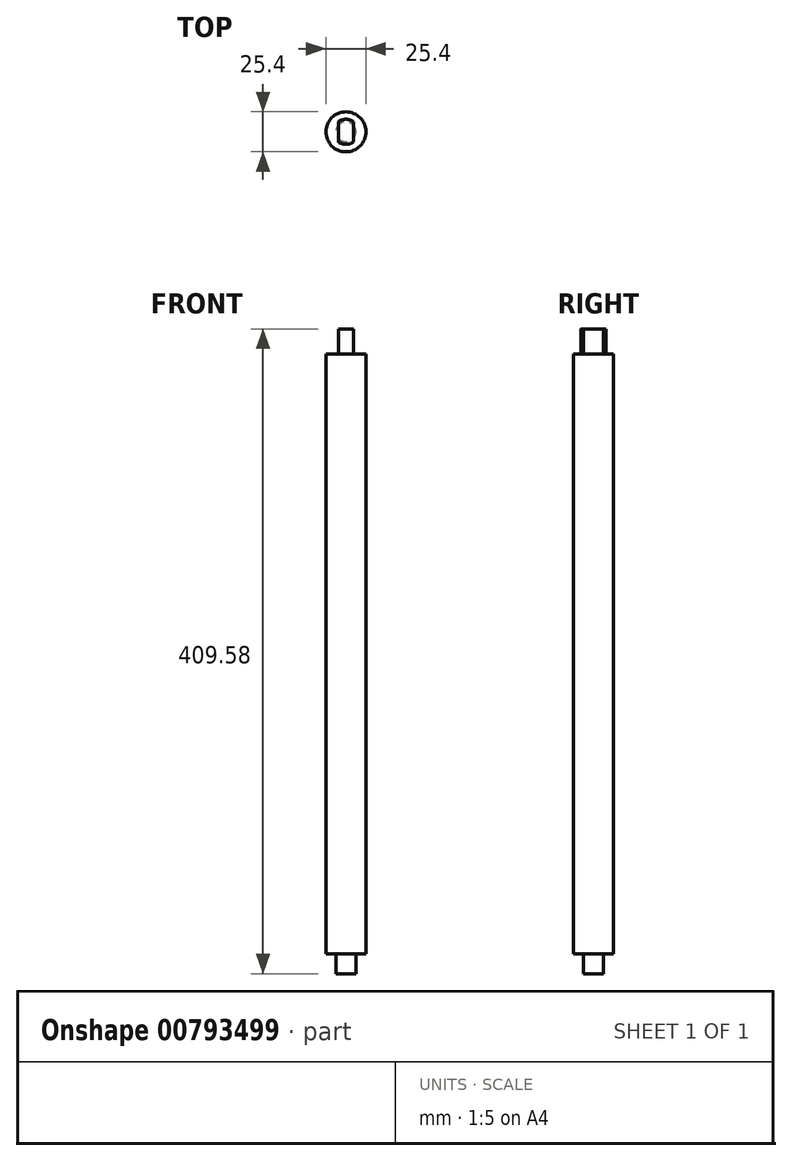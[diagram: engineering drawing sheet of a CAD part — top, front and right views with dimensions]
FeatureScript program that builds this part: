
annotation { "Feature Type Name" : "Feature", "Feature Type Description" : "" }
export const myFeature = defineFeature(function(context is Context, id is Id, definition is map)
    precondition{}
    {
        {
            var Q0;
            Q0=qCreatedBy(makeId("Top.planeOp"),FACE);
            var sketch = newSketch(context, id + "F0", { "sketchPlane" : qUnion([Q0])});
            skCircle(sketch, "E0", {"center": v(0, 0) * mm, "radius": 12.7 * mm});
            skSolve(sketch);
        }
        {
            var Q0;
            Q0 = qSketchRegion(id + "F0", true);
            extrude(context, id + "F1", {"entities" : qUnion([Q0]), "depth" : 381 * mm, "offsetDistance" : 25.4 * mm});
        }
        {
            var Q0;
            Q0=makeQuery(id+"F1.opExtrude","CAP_FACE",FACE,{"disambiguationData":[OSD([sQuery(id+"F0.wireOp",EDGE,"E0")])],"isStart":false});
            var sketch = newSketch(context, id + "F2", { "sketchPlane" : qUnion([Q0])});
            skCircle(sketch, "E1", {"center": v(0, 0) * mm, "radius": 7.94 * mm});
            skLineSegment(sketch, "E2.top", {"start": v(-4.76, 6.35) * mm, "end": v(4.76, 6.35) * mm});
            skLineSegment(sketch, "E2.left", {"start": v(-4.76, 0) * mm, "end": v(-4.76, 6.35) * mm});
            skLineSegment(sketch, "E2.right", {"start": v(4.76, 0) * mm, "end": v(4.76, 6.35) * mm});
            skLineSegment(sketch, "E3.MirrorCS", {"start": v(-4.76, 0) * mm, "end": v(-4.76, -6.35) * mm});
            skLineSegment(sketch, "E4.MirrorCS", {"start": v(-4.76, -6.35) * mm, "end": v(4.76, -6.35) * mm});
            skLineSegment(sketch, "E5.MirrorCS", {"start": v(4.76, 0) * mm, "end": v(4.76, -6.35) * mm});
            skSolve(sketch);
        }
        {
            var Q0;
            {var subQ0=sQuery(id+"F2.wireOp",EDGE,"E4.MirrorCS");Q0=makeQuery(id+"F2.imprint","IMPRINT",FACE,{"disambiguationData":[TD([[makeQuery(id+"F2.imprint","IMPRINT",EDGE,{"derivedFrom":subQ0}),-1.0]])]});}
            var Q1;
            Q1=makeQuery(id+"F2.imprint","IMPRINT",FACE,{"disambiguationData":[TD([[makeQuery(id+"F2.imprint","IMPRINT",EDGE,{"derivedFrom":sQuery(id+"F2.wireOp",EDGE,"E2.top")}),-1.0]])]});
            var Q2;
            {var subQ0=sQuery(id+"F2.wireOp",EDGE,"E2.top");Q2=makeQuery(id+"F2.imprint","IMPRINT",FACE,{"disambiguationData":[TD([[makeQuery(id+"F2.imprint","IMPRINT",EDGE,{"derivedFrom":subQ0}),1.0]])]});}
            extrude(context, id + "F3", {"entities" : qUnion([Q0, Q1, Q2]), "operationType" : NewBodyOperationType.ADD, "depth" : 15.88 * mm, "offsetDistance" : 25.4 * mm});
        }
        {
            var Q0;
            Q0=makeQuery(id+"F1.opExtrude","CAP_FACE",FACE,{"disambiguationData":[OSD([sQuery(id+"F0.wireOp",EDGE,"E0")])],"isStart":true});
            var sketch = newSketch(context, id + "F4", { "sketchPlane" : qUnion([Q0])});
            skCircle(sketch, "E6", {"center": v(0, 0) * mm, "radius": 6.35 * mm});
            skSolve(sketch);
        }
        {
            var Q0;
            Q0 = qSketchRegion(id + "F4", true);
            extrude(context, id + "F5", {"entities" : qUnion([Q0]), "operationType" : NewBodyOperationType.ADD, "depth" : 12.7 * mm, "offsetDistance" : 25.4 * mm});
        }
    });
